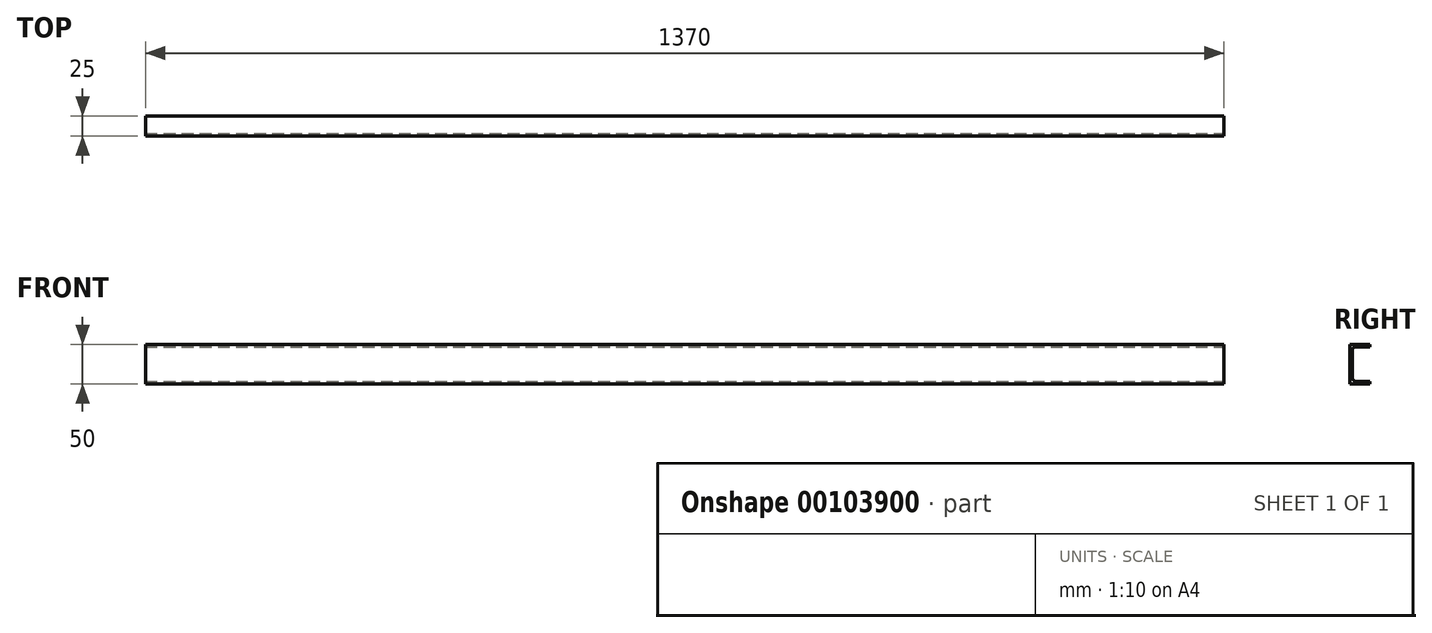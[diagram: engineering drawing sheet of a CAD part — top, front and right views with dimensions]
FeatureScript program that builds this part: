
annotation { "Feature Type Name" : "Feature", "Feature Type Description" : "" }
export const myFeature = defineFeature(function(context is Context, id is Id, definition is map)
    precondition{}
    {
        {
            var Q0;
            Q0=qCreatedBy(makeId("Right.planeOp"),FACE);
            var sketch = newSketch(context, id + "F0", { "sketchPlane" : qUnion([Q0])});
            skLineSegment(sketch, "E0.bottom", {"start": v(0, 0) * mm, "end": v(25, 0) * mm});
            skLineSegment(sketch, "E0.top", {"start": v(0, 50) * mm, "end": v(25, 50) * mm});
            skLineSegment(sketch, "E0.left", {"start": v(0, 0) * mm, "end": v(0, 50) * mm});
            skLineSegment(sketch, "E0.right", {"start": v(25, 0) * mm, "end": v(25, 3) * mm});
            skLineSegment(sketch, "E1.0", {"start": v(8, 47) * mm, "end": v(25, 47) * mm});
            skLineSegment(sketch, "E1.1", {"start": v(3, 8) * mm, "end": v(3, 42) * mm});
            skLineSegment(sketch, "E1.2", {"start": v(8, 3) * mm, "end": v(25, 3) * mm});
            skPoint(sketch, "E2.visualSharp", {"position": v(3, 47) * mm});
            skArc(sketch, "E2.filletArc", {"start": v(8, 47) * mm, "mid": v(4.46, 45.54) * mm, "end": v(3, 42) * mm});
            skPoint(sketch, "E3.visualSharp", {"position": v(3, 3) * mm});
            skArc(sketch, "E3.filletArc", {"start": v(3, 8) * mm, "mid": v(4.46, 4.46) * mm, "end": v(8, 3) * mm});
            skLineSegment(sketch, "E4.trimOffspring", {"start": v(25, 47) * mm, "end": v(25, 50) * mm});
            skPoint(sketch, "E5.visualSharp", {"position": v(0, 50) * mm});
            skLineSegment(sketch, "E5.filletArc", {"start": v(0, 50) * mm, "end": v(0, 50) * mm});
            skPoint(sketch, "E6.visualSharp", {"position": v(0, 0) * mm});
            skLineSegment(sketch, "E6.filletArc", {"start": v(0, 0) * mm, "end": v(0, 0) * mm});
            skPoint(sketch, "E7.visualSharp", {"position": v(25, 0) * mm});
            skLineSegment(sketch, "E7.filletArc", {"start": v(25, 0) * mm, "end": v(25, 0) * mm});
            skPoint(sketch, "E8.visualSharp", {"position": v(25, 3) * mm});
            skLineSegment(sketch, "E8.filletArc", {"start": v(25, 3) * mm, "end": v(25, 3) * mm});
            skPoint(sketch, "E9.visualSharp", {"position": v(25, 47) * mm});
            skLineSegment(sketch, "E9.filletArc", {"start": v(25, 47) * mm, "end": v(25, 47) * mm});
            skPoint(sketch, "E10.visualSharp", {"position": v(25, 50) * mm});
            skLineSegment(sketch, "E10.filletArc", {"start": v(25, 50) * mm, "end": v(25, 50) * mm});
            skSolve(sketch);
        }
        {
            var Q0;
            Q0 = qSketchRegion(id + "F0", true);
            extrude(context, id + "F1", {"entities" : qUnion([Q0]), "oppositeDirection" : true, "depth" : 1370 * mm});
        }
    });
